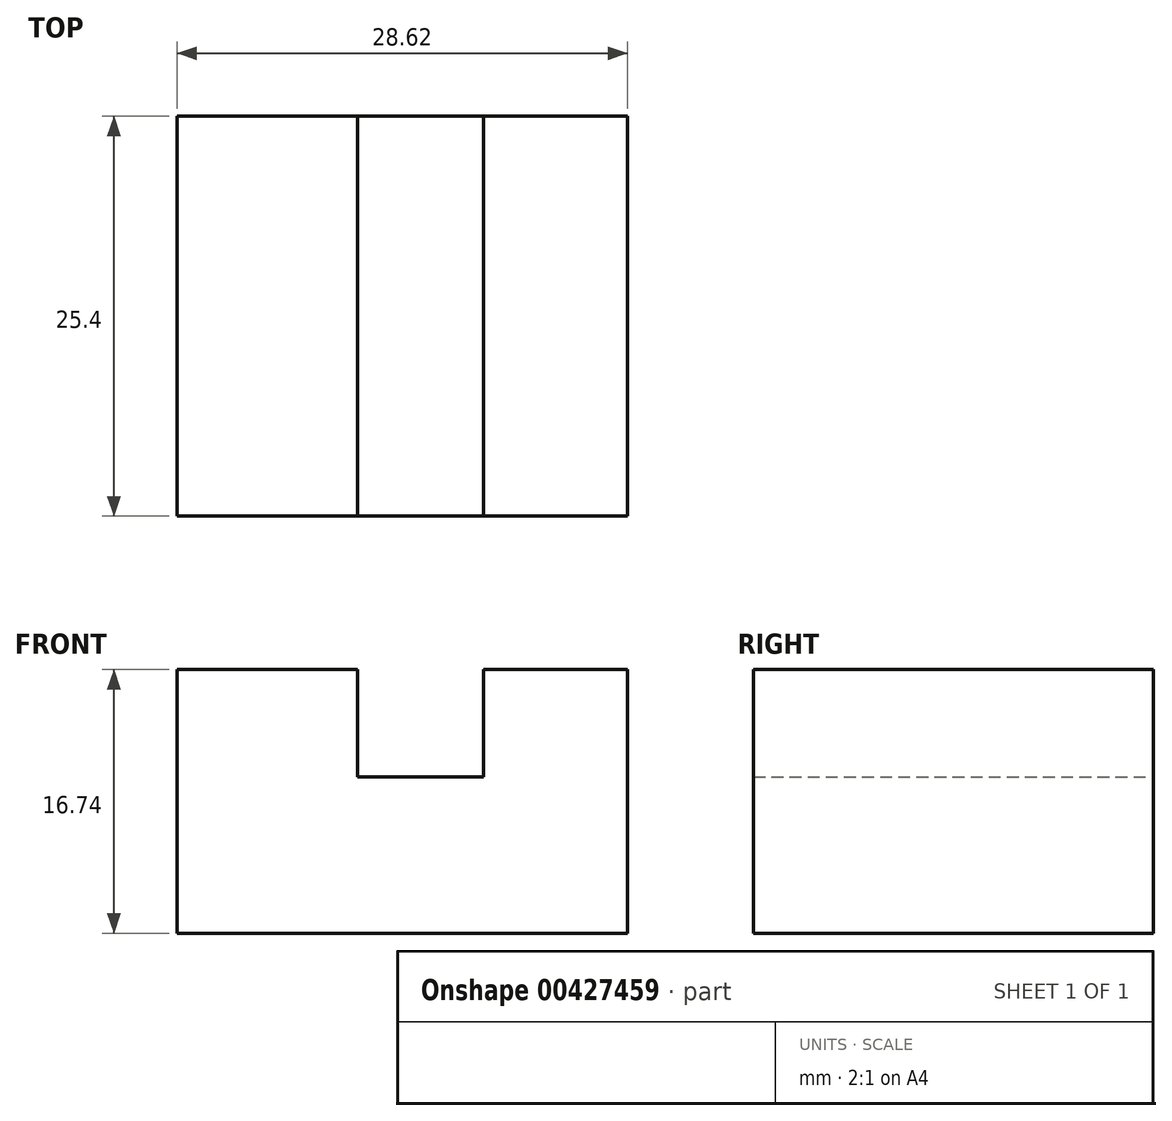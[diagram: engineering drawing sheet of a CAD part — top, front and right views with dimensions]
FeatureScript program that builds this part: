
annotation { "Feature Type Name" : "Feature", "Feature Type Description" : "" }
export const myFeature = defineFeature(function(context is Context, id is Id, definition is map)
    precondition{}
    {
        {
            var Q0;
            Q0=qCreatedBy(makeId("Front.planeOp"),FACE);
            var sketch = newSketch(context, id + "F0", { "sketchPlane" : qUnion([Q0])});
            skLineSegment(sketch, "E0", {"start": v(0, 0) * mm, "end": v(28.62, 0) * mm});
            skLineSegment(sketch, "E1", {"start": v(28.62, 0) * mm, "end": v(28.62, 16.74) * mm});
            skLineSegment(sketch, "E2", {"start": v(28.62, 16.74) * mm, "end": v(19.47, 16.74) * mm});
            skLineSegment(sketch, "E3", {"start": v(19.47, 16.74) * mm, "end": v(19.47, 9.93) * mm});
            skLineSegment(sketch, "E4", {"start": v(19.47, 9.93) * mm, "end": v(11.49, 9.93) * mm});
            skLineSegment(sketch, "E5", {"start": v(11.49, 9.93) * mm, "end": v(11.49, 16.74) * mm});
            skLineSegment(sketch, "E6", {"start": v(11.49, 16.74) * mm, "end": v(0, 16.74) * mm});
            skLineSegment(sketch, "E7", {"start": v(0, 16.74) * mm, "end": v(0, 0) * mm});
            skLineSegment(sketch, "E8", {"start": v(28.62, 6.03) * mm, "end": v(0, 6.03) * mm});
            skSolve(sketch);
        }
        {
            var Q0;
            {var subQ0=sQuery(id+"F0.wireOp",EDGE,"E0");Q0=makeQuery(id+"F0.imprint","IMPRINT",FACE,{"disambiguationData":[TD([[makeQuery(id+"F0.imprint","IMPRINT",EDGE,{"derivedFrom":subQ0}),1.0]])]});}
            var Q1;
            {var subQ0=sQuery(id+"F0.wireOp",EDGE,"E2");Q1=makeQuery(id+"F0.imprint","IMPRINT",FACE,{"disambiguationData":[TD([[makeQuery(id+"F0.imprint","IMPRINT",EDGE,{"derivedFrom":subQ0}),1.0]])]});}
            extrude(context, id + "F1", {"entities" : qUnion([Q0, Q1]), "depth" : 25.4 * mm});
        }
    });
